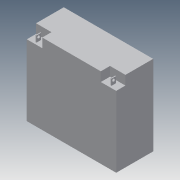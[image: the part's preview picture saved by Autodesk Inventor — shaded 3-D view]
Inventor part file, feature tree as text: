
AUTODESK INVENTOR PART (.ipt)
format: ipt  version: 2014 (Build 180170000, 170)  size: 118,272 bytes
history: native  units: in
note: dims shown in document units (in); Inventor stores cm internally (conversion verified against a paired STEP export)
features: extrude x5, sketch x5, projected_geometry x1
ambient origin geometry x8: Origin, YZ Plane, XZ Plane, XY Plane, X Axis, Y Axis, Z Axis, Center Point
bodies: Solid1 (feature_tree)
feature tree (11):
  extrude  "Extrusion1"  Depth=6.5in
  extrude  "Extrusion2"  Depth=0.75in
  extrude  "Extrusion3"  Depth=0.75in TaperAngle=0.0deg
  extrude  "Extrusion4"  Depth=0.375in
  extrude  "Extrusion5"  Depth=0.5in
  sketch  "Sketch1"  dims[d0=7.25in d1=6.5in]
  sketch  "Sketch2"  dims[d2=3.0in d3=0.0in d4=0.75in]
  sketch  "Sketch3"  dims[d5=1.25in d6=0.75in d7=0.0in]
  projected_geometry  "Projected Loop1"
  sketch  "Sketch4"  dims[d8=0.07in d9=0.375in]
  sketch  "Sketch5"  dims[d10=0.5in d11=0.0in d12=0.2362in d13=0.175in d14=0.5in d15=0.0in d16=0.2362in d17=0.175in d18=0.5in d19=0.0in]
